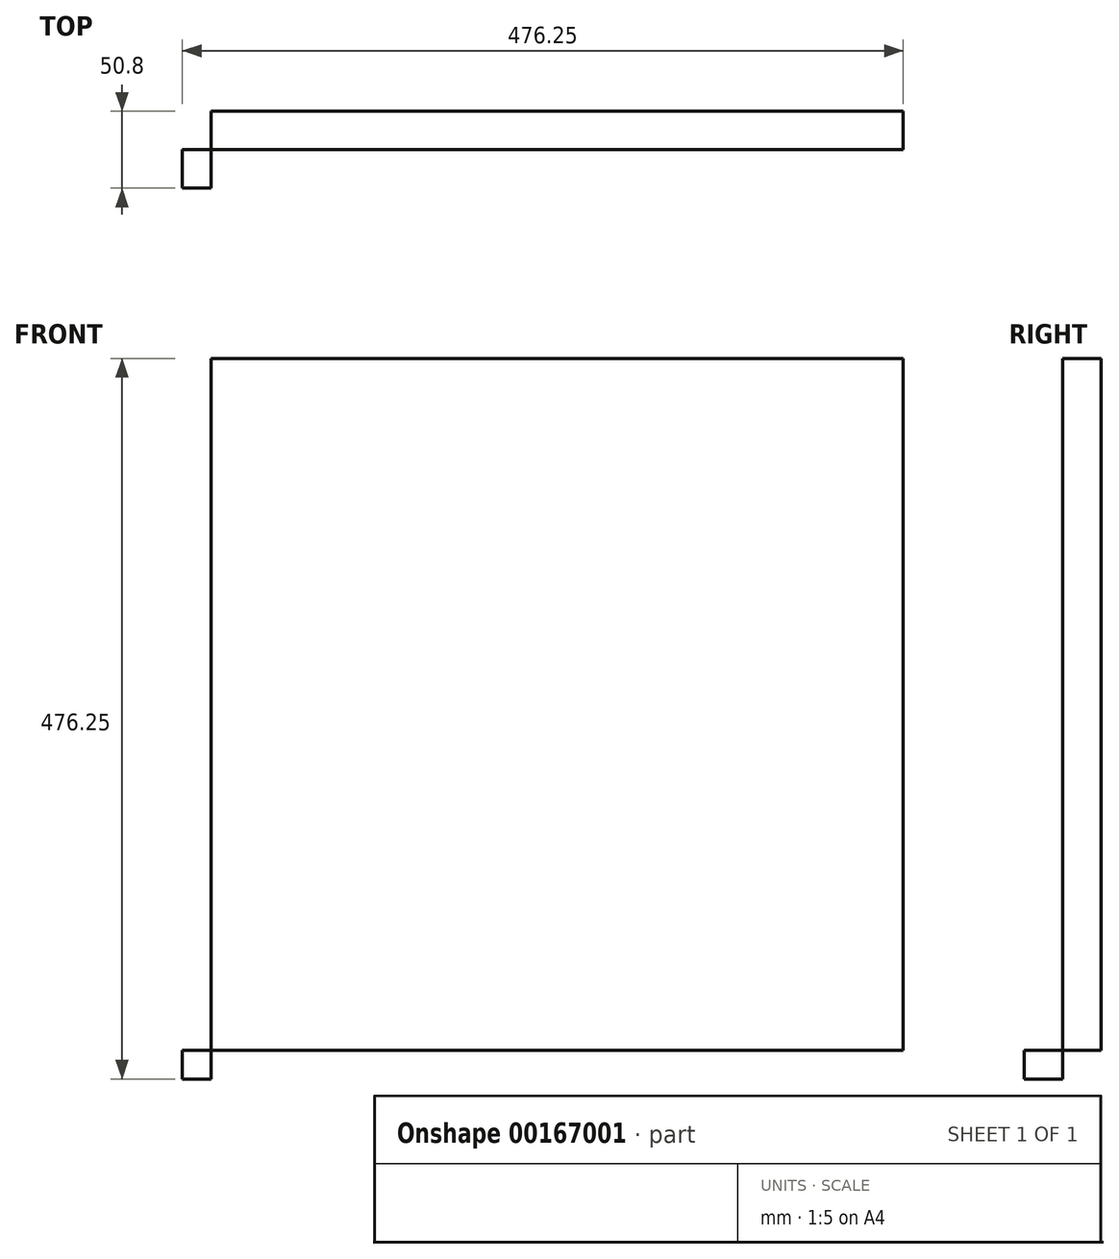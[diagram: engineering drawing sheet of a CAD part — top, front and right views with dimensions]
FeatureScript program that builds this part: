
annotation { "Feature Type Name" : "Feature", "Feature Type Description" : "" }
export const myFeature = defineFeature(function(context is Context, id is Id, definition is map)
    precondition{}
    {
        {
            var Q0;
            Q0=qCreatedBy(makeId("Front.planeOp"),FACE);
            var sketch = newSketch(context, id + "F0", { "sketchPlane" : qUnion([Q0])});
            skLineSegment(sketch, "E0.bottom", {"start": v(0, 0) * mm, "end": v(457.2, 0) * mm});
            skLineSegment(sketch, "E0.top", {"start": v(0, 457.2) * mm, "end": v(457.2, 457.2) * mm});
            skLineSegment(sketch, "E0.left", {"start": v(0, 0) * mm, "end": v(0, 457.2) * mm});
            skLineSegment(sketch, "E0.right", {"start": v(457.2, 0) * mm, "end": v(457.2, 457.2) * mm});
            skSolve(sketch);
        }
        {
            var Q0;
            Q0=makeQuery(id+"F0.imprint","IMPRINT",FACE,{"disambiguationData":[TD([[makeQuery(id+"F0.imprint","IMPRINT",EDGE,{"derivedFrom":sQuery(id+"F0.wireOp",EDGE,"E0.bottom")}),1.0]])]});
            extrude(context, id + "F1", {"entities" : qUnion([Q0]), "depth" : 25.4 * mm});
        }
        {
            var Q0;
            Q0=makeQuery(id+"F1.opExtrude","CAP_FACE",FACE,{"disambiguationData":[OSD([sQuery(id+"F0.wireOp",EDGE,"E0.bottom"),sQuery(id+"F0.wireOp",EDGE,"E0.top"),sQuery(id+"F0.wireOp",EDGE,"E0.left"),sQuery(id+"F0.wireOp",EDGE,"E0.right")])],"isStart":false});
            var sketch = newSketch(context, id + "F2", { "sketchPlane" : qUnion([Q0])});
            skLineSegment(sketch, "E1", {"start": v(0, 0) * mm, "end": v(-19.05, 0) * mm});
            skLineSegment(sketch, "E2", {"start": v(-19.05, 0) * mm, "end": v(-19.05, -19.05) * mm});
            skLineSegment(sketch, "E3", {"start": v(-19.05, -19.05) * mm, "end": v(0, -19.05) * mm});
            skLineSegment(sketch, "E4", {"start": v(0, -19.05) * mm, "end": v(0, 0) * mm});
            skSolve(sketch);
        }
        {
            var Q0;
            Q0=makeQuery(id+"F2.imprint","IMPRINT",FACE,{"disambiguationData":[TD([[makeQuery(id+"F2.imprint","IMPRINT",EDGE,{"derivedFrom":sQuery(id+"F2.wireOp",EDGE,"E1")}),1.0]])]});
            extrude(context, id + "F3", {"entities" : qUnion([Q0]), "depth" : 25.4 * mm});
        }
    });
